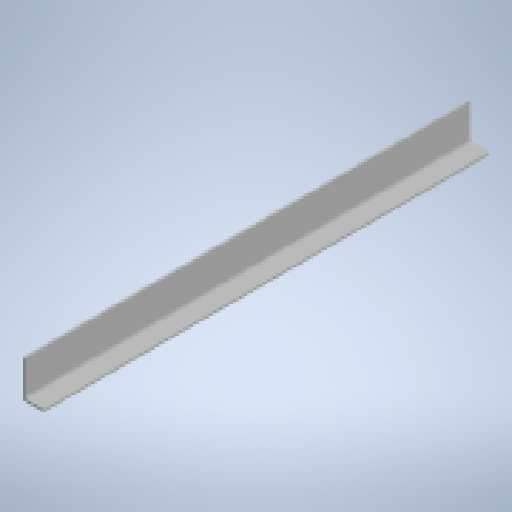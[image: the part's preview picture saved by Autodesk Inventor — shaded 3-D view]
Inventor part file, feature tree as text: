
AUTODESK INVENTOR PART (.ipt)
format: ipt  version: 2023 (Build 270158000, 158)  size: 140,288 bytes
history: native  units: in
note: dims shown in document units (in); Inventor stores cm internally (conversion verified against a paired STEP export)
features: extrude x1, sketch x1
ambient origin geometry x8: Origin, YZ Plane, XZ Plane, XY Plane, X Axis, Y Axis, Z Axis, Center Point
bodies: Solid1 (feature_tree)
feature tree (2):
  extrude  "Extrusion1"  Depth=1.75in
  sketch  "Sketch1"  dims[d0=0.188in d1=1.75in d2=3.0in d3=0.188in d4=36.25in d5=0.0in]
